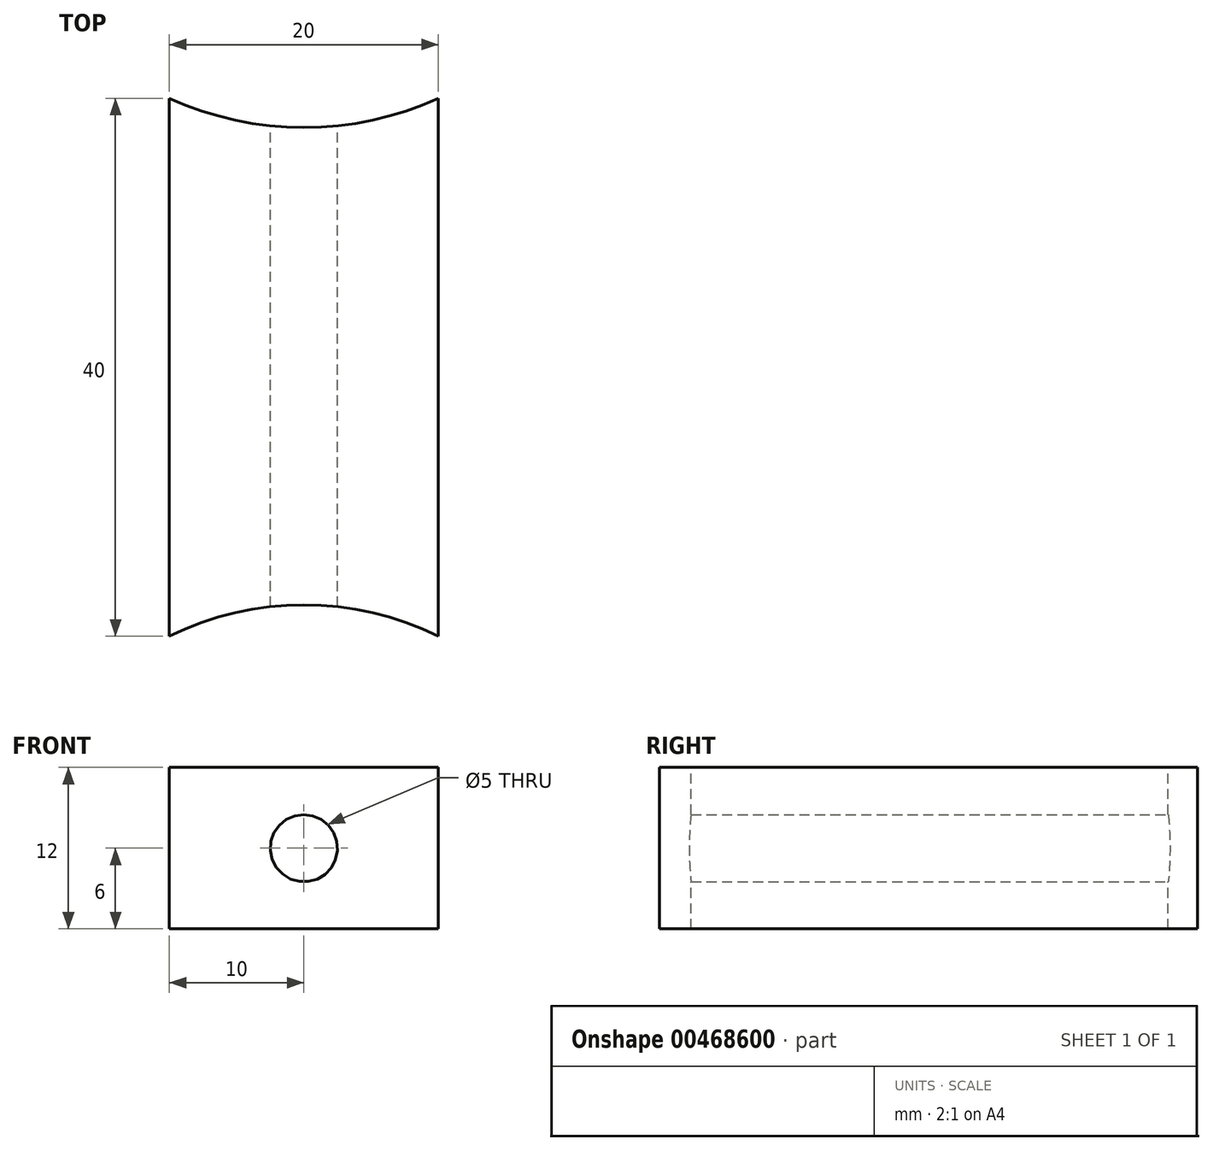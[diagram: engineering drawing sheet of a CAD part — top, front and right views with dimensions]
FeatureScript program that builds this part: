
annotation { "Feature Type Name" : "Feature", "Feature Type Description" : "" }
export const myFeature = defineFeature(function(context is Context, id is Id, definition is map)
    precondition{}
    {
        {
            var Q0;
            Q0=qCreatedBy(makeId("Front.planeOp"),FACE);
            var sketch = newSketch(context, id + "F0", { "sketchPlane" : qUnion([Q0])});
            skLineSegment(sketch, "E0.bottom", {"start": v(10, -6) * mm, "end": v(-10, -6) * mm});
            skLineSegment(sketch, "E0.top", {"start": v(10, 6) * mm, "end": v(-10, 6) * mm});
            skLineSegment(sketch, "E0.left", {"start": v(10, -6) * mm, "end": v(10, 6) * mm});
            skLineSegment(sketch, "E0.right", {"start": v(-10, -6) * mm, "end": v(-10, 6) * mm});
            skPoint(sketch, "E0.middle", {"position": v(0, 0) * mm});
            skSolve(sketch);
        }
        {
            var Q0;
            Q0=makeQuery(id+"F0.imprint","IMPRINT",FACE,{"disambiguationData":[TD([[makeQuery(id+"F0.imprint","IMPRINT",EDGE,{"derivedFrom":sQuery(id+"F0.wireOp",EDGE,"E0.bottom")}),-1.0]])]});
            extrude(context, id + "F1", {"entities" : qUnion([Q0]), "depth" : 40 * mm});
        }
        {
            var Q0;
            Q0=makeQuery(id+"F1.opExtrude","SWEPT_FACE",FACE,{"disambiguationData":[OSD([sQuery(id+"F0.wireOp",EDGE,"E0.top")])]});
            var sketch = newSketch(context, id + "F2", { "sketchPlane" : qUnion([Q0])});
            skArc(sketch, "E1", {"start": v(-10, 0) * mm, "mid": v(0, -2.18) * mm, "end": v(10, 0) * mm});
            skArc(sketch, "E2", {"start": v(10, -40) * mm, "mid": v(0, -37.66) * mm, "end": v(-10, -40) * mm});
            skLineSegment(sketch, "E3", {"start": v(-10, 0) * mm, "end": v(10, 0) * mm});
            skLineSegment(sketch, "E4", {"start": v(-10, -40) * mm, "end": v(10, -40) * mm});
            skSolve(sketch);
        }
        {
            var Q0;
            Q0=qSketchRegion(id+"F2",true);
            extrude(context, id + "F3", {"entities" : qUnion([Q0]), "operationType" : NewBodyOperationType.REMOVE, "oppositeDirection" : true, "depth" : 16 * mm});
        }
        {
            var Q0;
            Q0=qCreatedBy(makeId("Front.planeOp"),FACE);
            var sketch = newSketch(context, id + "F4", { "sketchPlane" : qUnion([Q0])});
            skPoint(sketch, "E5", {"position": v(0, 0) * mm});
            skSolve(sketch);
        }
        {
            var Q0;
            Q0=sQuery(id+"F4.wireOp",VERTEX,"E5");
            var Q1;
            Q1=makeQuery(id+"F1.opExtrude","SWEPT_BODY",BODY,{"disambiguationData":[OSD([sQuery(id+"F0.wireOp",EDGE,"E0.bottom"),sQuery(id+"F0.wireOp",EDGE,"E0.top"),sQuery(id+"F0.wireOp",EDGE,"E0.left"),sQuery(id+"F0.wireOp",EDGE,"E0.right")])]});
            hole(context, id + "F5", {"style" : HoleStyle.SIMPLE, "endStyle" : HoleEndStyle.THROUGH, "oppositeDirection" : true, "holeDiameter" : 5 * mm, "locations" : qUnion([Q0]), "scope" : qUnion([Q1]), "isTappedThrough" : true});
        }
    });
